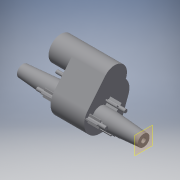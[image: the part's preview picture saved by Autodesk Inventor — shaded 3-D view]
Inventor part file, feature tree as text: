
AUTODESK INVENTOR PART (.ipt)
format: ipt  version: 2019 (Build 230136000, 136)  size: 268,800 bytes
history: native  units: in
note: dims shown in document units (in); Inventor stores cm internally (conversion verified against a paired STEP export)
features: sketch x8, extrude x6, pattern_circular x2, plane x1, loft x1, mirror x1
ambient origin geometry x8: Origin, YZ Plane, XZ Plane, XY Plane, X Axis, Y Axis, Z Axis, Center Point
bodies: Solid1 (feature_tree)
feature tree (19):
  extrude  "Extrusion1"  Depth=1.73in
  extrude  "Extrusion2"  Depth=1.5in
  sketch  "Sketch3"  dims[d5=1.05in d6=2.385in d7=0.0in]
  plane  "Work Plane1"
  loft  "Loft1"
  extrude  "Extrusion3"  Depth=1.15in TaperAngle=0.0deg
  extrude  "Extrusion4"  Depth=0.825in
  extrude  "Extrusion5"  TaperAngle=0.0deg  [1 undecoded]
  pattern_circular  "Circular Pattern2"  Angle=15.0deg  [1 undecoded]
  pattern_circular  "Circular Pattern1"  [2 undecoded]
  mirror  "Mirror1"
  extrude  "Extrusion6"  Depth=1.25in TaperAngle=0.0deg
  sketch  "Sketch1"  dims[d0=2.25in d1=1.73in]
  sketch  "Sketch2"  dims[d3=2.075in d4=1.5in]
  sketch  "Sketch4"  dims[d8=1.15in d9=0.9in d10=0.0in]
  sketch  "Sketch5"  dims[d11=2.2in d12=0.825in]
  sketch  "Sketch6"  dims[d13=0.0in d14=90.0deg d15=0.0in d16=90.0deg]
  sketch  "Sketch7"  dims[d17=0.33in]
  sketch  "Sketch8"  dims[d18=0.5in d19=0.0in d20=15.0deg d21=0.235in d23=1.25in d24=0.0in d25=1.1811in d26=360.0deg d29=0.075in d30=0.8in d31=0.0in d32=1.5748in d33=360.0deg d35=1.45in d36=0.0in d37=0.786in]
note: 4 required parameter values undecoded (feature->parameter linkage not recoverable at this tier; creation-order binding heuristic only, values carry confidence <= 0.55)
